# Revit family: QF_BOURGEAT_Self_Meuble_neutre_GN4
name_source: partatom
category: Equipement spécialisé
revit_build: Autodesk Revit 2015 (Build: 20140606_1530(x64)
units: mm (PartAtom-declared; Revit-internal decimal feet)

## types (16) — shared parameters
Certification = NF alimentaire
Charge max = 150.00 kg
Fabricant = BOURGEAT
Indice de protection = 21
Longueur hors tout = 1534 mm  [stored 5.03281 ft]
Nature isolant = Laine de verre
Profondeur hors tout = 820 mm
Spécification du Fabricant = Meuble_neutre_OASIS
URL catalogue = http://www.bourgeat.fr
lg_etagere = 1062 mm  [stored 3.48425 ft]
lg_presentoir = 1422 mm  [stored 4.66535 ft]
lgconsole = 1490 mm  [stored 4.88845 ft]
lgmeuble = 1466 mm

## per-type parameters (varying)
| type | Etageres | Fréquence | Hauteur hors tout | Intensité nominale | Modèle | Phase | Pieds | Poids net à vide | Presentoir | Puissance électrique  | Roues | Tension | dessus_decoupe | dessus_plat |
| GN4_dessus_decoupe | Non | 0 Hz | 900 mm | 0 A | 854224 | 0 | Oui | 150.00 kg | Non | 0 W | Non | 0 V | Oui | Non |
| GN4_dessus_plat | Non | 0 Hz | 900 mm | 0 A | 854114 | 0 | Oui | 150.00 kg | Non | 0 W | Non | 0 V | Non | Oui |
| GN4_dessus_plat+rampe_chauffante | Non | 50 Hz | 1330 mm | 3 A | 854114+851324 | 2 | Oui | 170.00 kg | Oui | 640 W | Non | 230 V | Non | Oui |
| GN4_dessus_plat+roues | Non | 0 Hz | 900 mm | 0 A | 854114+854950 | 0 | Non | 150.00 kg | Non | 0 W | Oui | 0 V | Non | Oui |
| GN4_dessus_plat+etageres | Oui | 0 Hz | 900 mm | 0 A | 854114+854954 | 0 | Oui | 150.00 kg | Non | 0 W | Non | 0 V | Non | Oui |
| GN4_dessus_plat+rampe_chauffante+roues | Non | 50 Hz | 1330 mm | 3 A | 854114+851324+854950 | 2 | Non | 170.00 kg | Oui | 640 W | Oui | 230 V | Non | Oui |
| GN4_dessus_plat+rampe_chauffante+etageres | Oui | 50 Hz | 1330 mm | 3 A | 854114+851324+854954 | 2 | Oui | 170.00 kg | Oui | 640 W | Non | 230 V | Non | Oui |
| GN4_dessus_plat+roues+etageres | Oui | 0 Hz | 900 mm | 0 A | 854114+854950+854954 | 0 | Non | 150.00 kg | Non | 0 W | Oui | 0 V | Non | Oui |
| GN4_dessus_plat+rampe_chauffante+roues+etageres | Oui | 50 Hz | 1330 mm | 3 A | 854114+851324+854950+854954 | 2 | Non | 170.00 kg | Oui | 640 W | Oui | 230 V | Non | Oui |
| GN4_dessus_decoupe+presentoir_chauffant | Non | 50 Hz | 1330 mm | 3 A | 854224+851324 | 2 | Oui | 170.00 kg | Oui | 640 W | Non | 230 V | Oui | Non |
| GN4_dessus_decoupe+roues | Non | 0 Hz | 900 mm | 0 A | 854224+854950 | 0 | Non | 150.00 kg | Non | 0 W | Oui | 0 V | Oui | Non |
| GN4_dessus_decoupe+etageres | Oui | 0 Hz | 900 mm | 0 A | 854224+854954 | 0 | Oui | 150.00 kg | Non | 0 W | Non | 0 V | Oui | Non |
| GN4_dessus_decoupe+presentoir_chauffant+roues | Non | 50 Hz | 1330 mm | 3 A | 854224+851324+854950 | 2 | Non | 170.00 kg | Oui | 640 W | Oui | 230 V | Oui | Non |
| GN4_dessus_decoupe+presentoir_chauffant+etageres | Oui | 50 Hz | 1330 mm | 3 A | 854224+851324+854954 | 2 | Oui | 170.00 kg | Oui | 640 W | Non | 230 V | Oui | Non |
| GN4_dessus_decoupe+roues+etageres | Oui | 0 Hz | 900 mm | 0 A | 854224+854950+854954 | 0 | Non | 150.00 kg | Non | 0 W | Oui | 0 V | Oui | Non |
| GN4_dessus_decoupe+presentoir_chauffant+roues+etageres | Oui | 50 Hz | 1330 mm | 3 A | 854224+851324+854950+854954 | 2 | Non | 170.00 kg | Oui | 640 W | Oui | 230 V | Oui | Non |

note: [stored X ft] marks values corroborated as IEEE doubles in the binary element streams (Revit-internal decimal feet)

## geometry (parser evidence)
native form markers: Blend x12
no freeform markers — native parametric forms only
